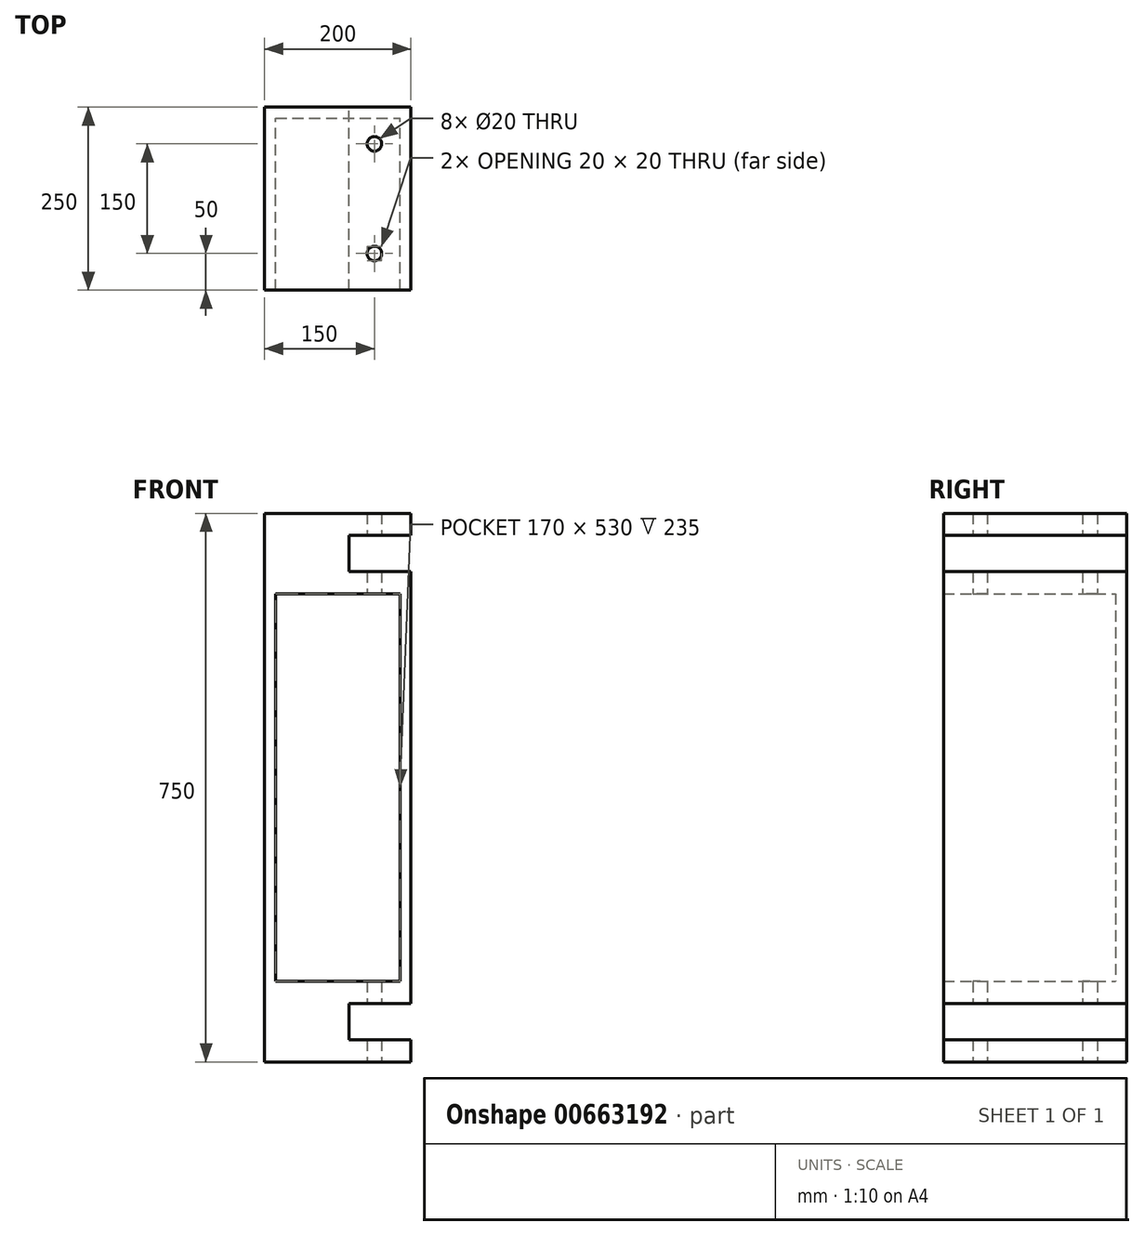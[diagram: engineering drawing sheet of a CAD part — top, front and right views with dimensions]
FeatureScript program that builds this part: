
annotation { "Feature Type Name" : "Feature", "Feature Type Description" : "" }
export const myFeature = defineFeature(function(context is Context, id is Id, definition is map)
    precondition{}
    {
        {
            var Q0;
            Q0=qCreatedBy(makeId("Front.planeOp"),FACE);
            var sketch = newSketch(context, id + "F0", { "sketchPlane" : qUnion([Q0])});
            skLineSegment(sketch, "E0.bottom", {"start": v(100, 375) * mm, "end": v(-100, 375) * mm});
            skLineSegment(sketch, "E0.top", {"start": v(100, -375) * mm, "end": v(-100, -375) * mm});
            skLineSegment(sketch, "E0.left", {"start": v(100, 375) * mm, "end": v(100, -375) * mm});
            skLineSegment(sketch, "E0.right", {"start": v(-100, 375) * mm, "end": v(-100, -375) * mm});
            skPoint(sketch, "E0.middle", {"position": v(0, 0) * mm});
            skLineSegment(sketch, "E1.bottom", {"start": v(-85, 265) * mm, "end": v(85, 265) * mm});
            skLineSegment(sketch, "E1.top", {"start": v(-85, -265) * mm, "end": v(85, -265) * mm});
            skLineSegment(sketch, "E1.left", {"start": v(-85, 265) * mm, "end": v(-85, -265) * mm});
            skLineSegment(sketch, "E1.right", {"start": v(85, 265) * mm, "end": v(85, -265) * mm});
            skLineSegment(sketch, "E2", {"start": v(100, 345) * mm, "end": v(15, 345) * mm});
            skLineSegment(sketch, "E3", {"start": v(15, 345) * mm, "end": v(15, 295) * mm});
            skLineSegment(sketch, "E4", {"start": v(15, 295) * mm, "end": v(100, 295) * mm});
            skLineSegment(sketch, "E5", {"start": v(100, -295) * mm, "end": v(15, -295) * mm});
            skLineSegment(sketch, "E6", {"start": v(15, -295) * mm, "end": v(15, -345) * mm});
            skLineSegment(sketch, "E7", {"start": v(15, -345) * mm, "end": v(100, -345) * mm});
            skSolve(sketch);
        }
        {
            var Q0;
            {var subQ3=sQuery(id+"F0.wireOp",EDGE,"E0.bottom");Q0=makeQuery(id+"F0.imprint","IMPRINT",FACE,{"disambiguationData":[TD([[makeQuery(id+"F0.imprint","IMPRINT",EDGE,{"derivedFrom":subQ3}),1.0]])]});}
            extrude(context, id + "F1", {"entities" : qUnion([Q0]), "depth" : 250 * mm, "offsetDistance" : 25 * mm});
        }
        {
            var Q0;
            Q0=makeQuery(id+"F0.imprint","IMPRINT",FACE,{"disambiguationData":[TD([[makeQuery(id+"F0.imprint","IMPRINT",EDGE,{"derivedFrom":sQuery(id+"F0.wireOp",EDGE,"E1.bottom")}),-1.0]])]});
            extrude(context, id + "F2", {"entities" : qUnion([Q0]), "operationType" : NewBodyOperationType.ADD, "depth" : 15 * mm, "offsetDistance" : 25 * mm});
        }
        {
            var Q0;
            Q0=makeQuery(id+"F1.opExtrude","SWEPT_FACE",FACE,{"disambiguationData":[OSD([sQuery(id+"F0.wireOp",EDGE,"E0.top")])]});
            var sketch = newSketch(context, id + "F3", { "sketchPlane" : qUnion([Q0])});
            skCircle(sketch, "E8", {"center": v(50, 200) * mm, "radius": 10 * mm});
            skCircle(sketch, "E9", {"center": v(50, 50) * mm, "radius": 10 * mm});
            skLineSegment(sketch, "E10", {"start": v(50, 200) * mm, "end": v(60, 200) * mm});
            skLineSegment(sketch, "E11", {"start": v(50, 50) * mm, "end": v(60, 50) * mm});
            skSolve(sketch);
        }
        {
            var Q0;
            Q0 = qSketchRegion(id + "F3", true);
            extrude(context, id + "F4", {"entities" : qUnion([Q0]), "operationType" : NewBodyOperationType.REMOVE, "oppositeDirection" : true, "depth" : 750 * mm, "offsetDistance" : 25 * mm});
        }
    });
